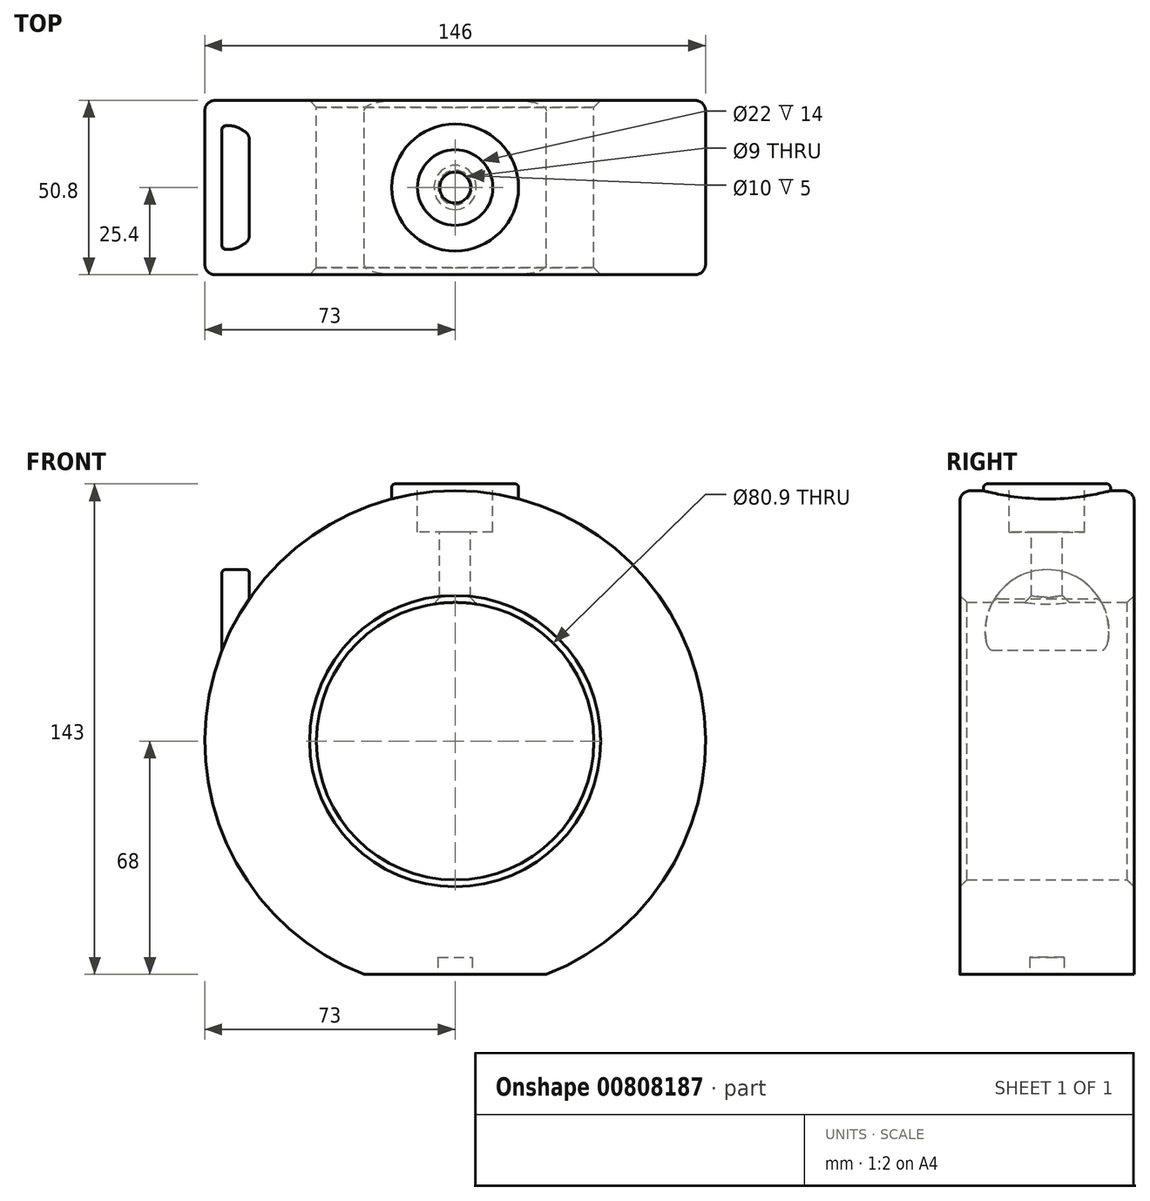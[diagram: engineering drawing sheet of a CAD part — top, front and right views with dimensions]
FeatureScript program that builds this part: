
annotation { "Feature Type Name" : "Feature", "Feature Type Description" : "" }
export const myFeature = defineFeature(function(context is Context, id is Id, definition is map)
    precondition{}
    {
        {
            var Q0;
            Q0=qCreatedBy(makeId("Front.planeOp"),FACE);
            var sketch = newSketch(context, id + "F0", { "sketchPlane" : qUnion([Q0])});
            skCircle(sketch, "E0", {"center": v(0, 0) * mm, "radius": 73 * mm});
            skCircle(sketch, "E1", {"center": v(0, 0) * mm, "radius": 40.45 * mm});
            skSolve(sketch);
        }
        {
            var Q0;
            Q0 = qSketchRegion(id + "F0", true);
            extrude(context, id + "F1", {"entities" : qUnion([Q0]), "depth" : 50.8 * mm, "offsetDistance" : 25 * mm});
        }
        {
            var Q0;
            Q0=makeQuery(id+"F1.opExtrude","SWEPT_FACE",FACE,{"disambiguationData":[OSD([sQuery(id+"F0.wireOp",EDGE,"E0")])]});
            fillet(context, id + "F2", {"entities" : qUnion([Q0]), "radius" : 3 * mm, "tangentPropagation" : true, "allowEdgeOverflow" : false});
        }
        {
            var Q0;
            Q0=qCreatedBy(makeId("Top.planeOp"),FACE);
            cPlane(context, id + "F3", {"entities" : qUnion([Q0]), "cplaneType" : CPlaneType.OFFSET, "offset" : 75 * mm, "width" : 150 * mm, "height" : 150 * mm});
        }
        {
            var Q0;
            Q0=qCreatedBy(id+"F3.planeOp",FACE);
            var sketch = newSketch(context, id + "F4", { "sketchPlane" : qUnion([Q0])});
            skLineSegment(sketch, "E2", {"start": v(-37.23, -25.4) * mm, "end": v(59.83, -25.4) * mm, "construction": true});
            skCircle(sketch, "E3", {"center": v(0, -25.4) * mm, "radius": 18.5 * mm});
            skSolve(sketch);
        }
        {
            var Q0;
            Q0 = qSketchRegion(id + "F4", true);
            var Q1;
            Q1=makeQuery(id+"F1.opExtrude","SWEPT_FACE",FACE,{"disambiguationData":[OSD([sQuery(id+"F0.wireOp",EDGE,"E0")])]});
            extrude(context, id + "F5", {"entities" : qUnion([Q0]), "operationType" : NewBodyOperationType.ADD, "endBound" : BoundingType.UP_TO_SURFACE, "oppositeDirection" : true, "depth" : 25 * mm, "endBoundEntityFace" : qUnion([Q1]), "offsetDistance" : 25 * mm});
        }
        {
            var Q0;
            Q0=makeQuery(id+"F5.opExtrude","CAP_EDGE",EDGE,{"disambiguationData":[OSD([sQuery(id+"F4.wireOp",EDGE,"E3")])],"isStart":true});
            var Q1;
            Q1=makeQuery(id+"F5.opExtrude","CAP_EDGE",EDGE,{"disambiguationData":[OSD([sQuery(id+"F4.wireOp",EDGE,"E3")])],"isStart":false});
            fillet(context, id + "F6", {"entities" : qUnion([Q0, Q1]), "radius" : 1 * mm, "tangentPropagation" : true, "allowEdgeOverflow" : false});
        }
        {
            var Q0;
            Q0=makeQuery(id+"F5.opExtrude","CAP_FACE",FACE,{"disambiguationData":[OSD([sQuery(id+"F4.wireOp",EDGE,"E3")])],"isStart":true});
            var sketch = newSketch(context, id + "F7", { "sketchPlane" : qUnion([Q0])});
            skCircle(sketch, "E4", {"center": v(0, -25.4) * mm, "radius": 11 * mm});
            skSolve(sketch);
        }
        {
            var Q0;
            Q0 = qSketchRegion(id + "F7", true);
            extrude(context, id + "F8", {"entities" : qUnion([Q0]), "operationType" : NewBodyOperationType.REMOVE, "oppositeDirection" : true, "depth" : 14 * mm, "offsetDistance" : 25 * mm});
        }
        {
            var Q0;
            Q0=makeQuery(id+"F8.boolean.opBoolean","COPY",FACE,{"derivedFrom":makeQuery(id+"F8.opExtrude","CAP_FACE",FACE,{"disambiguationData":[OSD([sQuery(id+"F7.wireOp",EDGE,"E4")])],"isStart":false})});
            var sketch = newSketch(context, id + "F9", { "sketchPlane" : qUnion([Q0])});
            skCircle(sketch, "E5", {"center": v(0, -25.4) * mm, "radius": 4.5 * mm});
            skSolve(sketch);
        }
        {
            var Q0;
            Q0 = qSketchRegion(id + "F9", true);
            extrude(context, id + "F10", {"entities" : qUnion([Q0]), "operationType" : NewBodyOperationType.REMOVE, "oppositeDirection" : true, "depth" : 31.3 * mm, "offsetDistance" : 25 * mm});
        }
        {
            var Q0;
            Q0=qCreatedBy(makeId("Top.planeOp"),FACE);
            cPlane(context, id + "F11", {"entities" : qUnion([Q0]), "cplaneType" : CPlaneType.OFFSET, "offset" : 68 * mm, "oppositeDirection" : true, "width" : 150 * mm, "height" : 150 * mm});
        }
        {
            var Q0;
            Q0=qCreatedBy(id+"F11.planeOp",FACE);
            var sketch = newSketch(context, id + "F12", { "sketchPlane" : qUnion([Q0])});
            skLineSegment(sketch, "E6", {"start": v(-8.4, -25.4) * mm, "end": v(31.47, -25.4) * mm, "construction": true});
            skLineSegment(sketch, "E7.bottom", {"start": v(40.37, 20.11) * mm, "end": v(-40.37, 20.11) * mm});
            skLineSegment(sketch, "E7.top", {"start": v(40.37, -70.91) * mm, "end": v(-40.37, -70.91) * mm});
            skLineSegment(sketch, "E7.left", {"start": v(40.37, 20.11) * mm, "end": v(40.37, -70.91) * mm});
            skLineSegment(sketch, "E7.right", {"start": v(-40.37, 20.11) * mm, "end": v(-40.37, -70.91) * mm});
            skPoint(sketch, "E7.middle", {"position": v(0, -25.4) * mm});
            skSolve(sketch);
        }
        {
            var Q0;
            Q0 = qSketchRegion(id + "F12", true);
            extrude(context, id + "F13", {"entities" : qUnion([Q0]), "operationType" : NewBodyOperationType.REMOVE, "oppositeDirection" : true, "depth" : 25 * mm, "offsetDistance" : 25 * mm});
        }
        {
            var Q0;
            Q0=makeQuery(id+"F13.boolean.opBoolean","COPY",FACE,{"derivedFrom":makeQuery(id+"F13.opExtrude","CAP_FACE",FACE,{"disambiguationData":[OSD([sQuery(id+"F12.wireOp",EDGE,"E7.bottom"),sQuery(id+"F12.wireOp",EDGE,"E7.top"),sQuery(id+"F12.wireOp",EDGE,"E7.left"),sQuery(id+"F12.wireOp",EDGE,"E7.right")])],"isStart":true})});
            var sketch = newSketch(context, id + "F14", { "sketchPlane" : qUnion([Q0])});
            skLineSegment(sketch, "E8", {"start": v(-22.08, 25.4) * mm, "end": v(26.24, 25.4) * mm, "construction": true});
            skLineSegment(sketch, "E9", {"start": v(0, 0) * mm, "end": v(0, 43.84) * mm, "construction": true});
            skCircle(sketch, "E10", {"center": v(0, 25.4) * mm, "radius": 5 * mm});
            skSolve(sketch);
        }
        {
            var Q0;
            Q0 = qSketchRegion(id + "F14", true);
            extrude(context, id + "F15", {"entities" : qUnion([Q0]), "operationType" : NewBodyOperationType.REMOVE, "oppositeDirection" : true, "depth" : 5 * mm, "offsetDistance" : 25 * mm});
        }
        {
            var Q0;
            Q0=makeQuery(id+"F1.opExtrude","SWEPT_FACE",FACE,{"disambiguationData":[OSD([sQuery(id+"F0.wireOp",EDGE,"E1")])]});
            chamfer(context, id + "F16", {"entities" : qUnion([Q0]), "width" : 2 * mm, "tangentPropagation" : true});
        }
        {
            var Q0;
            Q0=qCreatedBy(makeId("Right.planeOp"),FACE);
            cPlane(context, id + "F17", {"entities" : qUnion([Q0]), "cplaneType" : CPlaneType.OFFSET, "offset" : 68 * mm, "oppositeDirection" : true, "width" : 150 * mm, "height" : 150 * mm});
        }
        {
            var Q0;
            Q0=qCreatedBy(id+"F17.planeOp",FACE);
            var sketch = newSketch(context, id + "F18", { "sketchPlane" : qUnion([Q0])});
            skCircle(sketch, "E11", {"center": v(-25.4, 32) * mm, "radius": 18 * mm});
            skSolve(sketch);
        }
        {
            var Q0;
            Q0 = qSketchRegion(id + "F18", true);
            var Q1;
            Q1=makeQuery(id+"F1.opExtrude","SWEPT_FACE",FACE,{"disambiguationData":[OSD([sQuery(id+"F0.wireOp",EDGE,"E0")])]});
            var Q2;
            Q2=makeQuery(id+"F1.opExtrude","SWEPT_BODY",BODY,{"disambiguationData":[OSD([sQuery(id+"F0.wireOp",EDGE,"E0"),sQuery(id+"F0.wireOp",EDGE,"E1")])]});
            extrude(context, id + "F19", {"entities" : qUnion([Q0]), "operationType" : NewBodyOperationType.ADD, "depth" : 8 * mm, "endBoundEntityFace" : qUnion([Q1]), "endBoundEntityBody" : qUnion([Q2]), "offsetDistance" : 25 * mm});
        }
        {
            var Q0;
            Q0=makeQuery(id+"F19.opExtrude","CAP_EDGE",EDGE,{"disambiguationData":[OSD([sQuery(id+"F18.wireOp",EDGE,"E11")])],"isStart":true});
            var Q1;
            Q1=makeQuery(id+"F19.opExtrude","CAP_EDGE",EDGE,{"disambiguationData":[OSD([sQuery(id+"F18.wireOp",EDGE,"E11")])],"isStart":false});
            fillet(context, id + "F20", {"entities" : qUnion([Q0, Q1]), "radius" : 1 * mm, "tangentPropagation" : true, "allowEdgeOverflow" : false});
        }
    });
